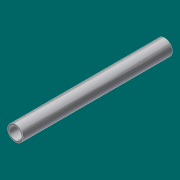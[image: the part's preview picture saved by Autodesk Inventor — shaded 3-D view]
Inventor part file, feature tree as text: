
AUTODESK INVENTOR PART (.ipt)
format: ipt  version: 2017 (Build 210142000, 142)  size: 121,344 bytes
history: native  units: in
note: dims shown in document units (in); Inventor stores cm internally (conversion verified against a paired STEP export)
features: extrude x1, sketch x1
ambient origin geometry x8: Origin, YZ Plane, XZ Plane, XY Plane, X Axis, Y Axis, Z Axis, Center Point
bodies: Solid1 (feature_tree)
feature tree (2):
  extrude  "Extrusion1"  Depth=18.25in
  sketch  "Sketch1"  dims[d0=1.9in d1=1.5in d2=18.25in d3=0.0in]
